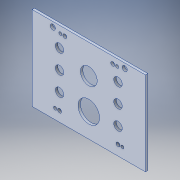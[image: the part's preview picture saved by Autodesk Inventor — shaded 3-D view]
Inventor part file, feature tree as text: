
AUTODESK INVENTOR PART (.ipt)
format: ipt  version: 2016 (Build 200138000, 138)  size: 263,680 bytes
history: native  units: in
note: dims shown in document units (in); Inventor stores cm internally (conversion verified against a paired STEP export)
features: extrude x5, sketch x5, projected_geometry x5, fillet x1
ambient origin geometry x8: Origin, YZ Plane, XZ Plane, XY Plane, X Axis, Y Axis, Z Axis, Center Point
bodies: Solid1 (feature_tree)
feature tree (16):
  extrude  "Extrusion1"  Depth=0.125in TaperAngle=0.0deg
  extrude  "Extrusion2"  Depth=0.405in TaperAngle=0.0deg
  extrude  "Extrusion5"  [1 undecoded]
  extrude  "Extrusion7"  [1 undecoded]
  extrude  "Extrusion8"  [1 undecoded]
  sketch  "Sketch1"  dims[d0=0.125in d1=0.0in d2=0.125in d3=0.0in]
  projected_geometry  "Projected Loop1"
  sketch  "Sketch2"  dims[d8=0.146in d9=0.0in d14=0.405in d15=0.0in]
  projected_geometry  "Projected Loop2"
  sketch  "Sketch5"  dims[d16=0.405in d17=0.0in]
  projected_geometry  "Projected Loop5"
  sketch  "Sketch8"
  projected_geometry  "Projected Loop8"
  sketch  "Sketch9"
  projected_geometry  "Projected Loop9"
  fillet  "Fillet5"  [1 undecoded]
note: 4 required parameter values undecoded (feature->parameter linkage not recoverable at this tier; creation-order binding heuristic only, values carry confidence <= 0.55)
